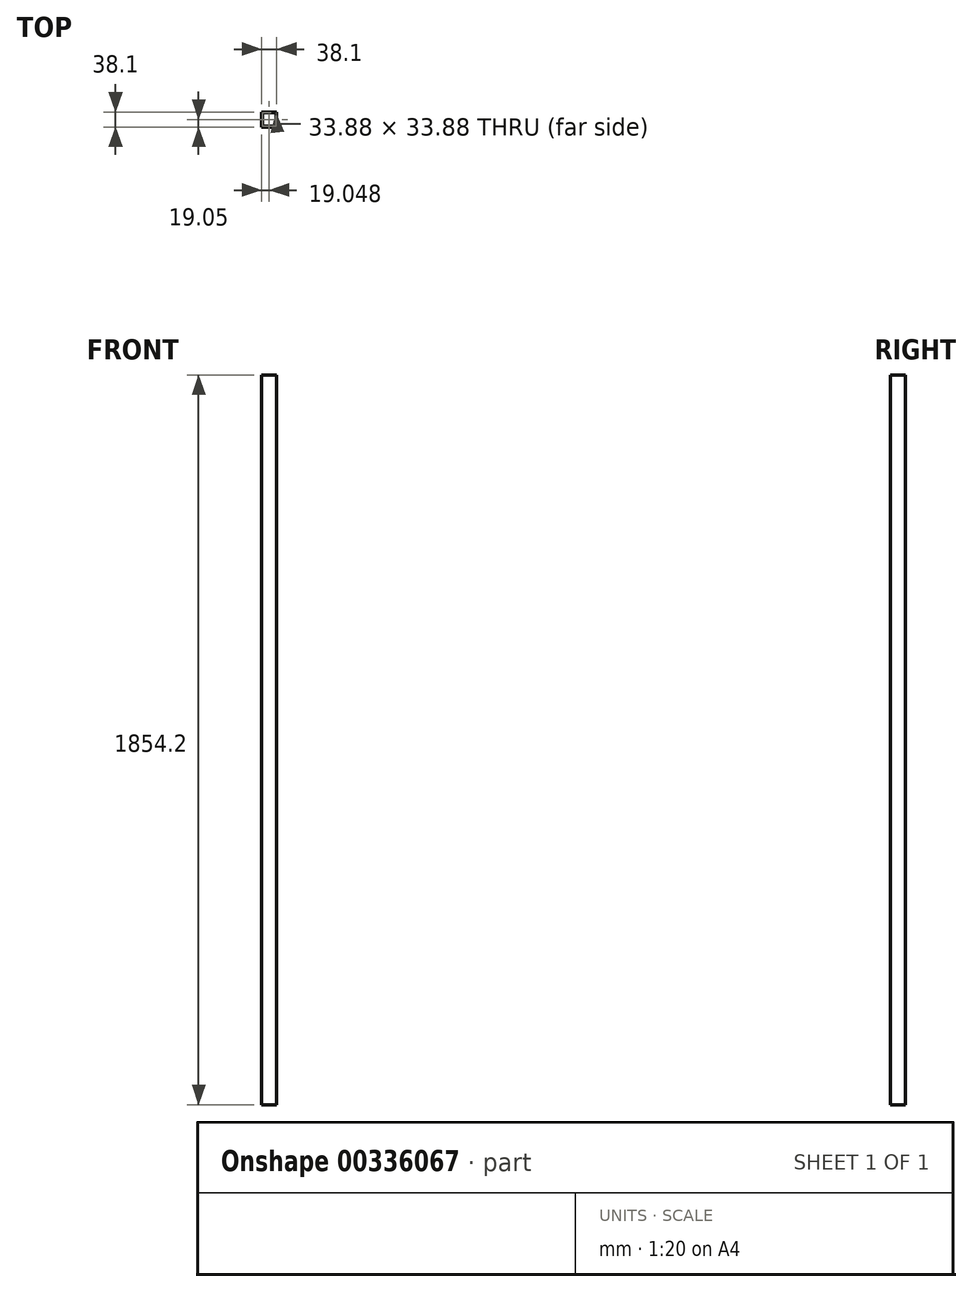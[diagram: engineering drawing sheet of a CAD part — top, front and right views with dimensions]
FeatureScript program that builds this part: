
annotation { "Feature Type Name" : "Feature", "Feature Type Description" : "" }
export const myFeature = defineFeature(function(context is Context, id is Id, definition is map)
    precondition{}
    {
        {
            var Q0;
            Q0=qCreatedBy(makeId("Front.planeOp"),FACE);
            var sketch = newSketch(context, id + "F0", { "sketchPlane" : qUnion([Q0])});
            skLineSegment(sketch, "E0.bottom", {"start": v(-146.7, 887.15) * mm, "end": v(-108.6, 887.15) * mm});
            skLineSegment(sketch, "E0.top", {"start": v(-146.7, -967.05) * mm, "end": v(-108.6, -967.05) * mm});
            skLineSegment(sketch, "E0.left", {"start": v(-146.7, 887.15) * mm, "end": v(-146.7, -967.05) * mm});
            skLineSegment(sketch, "E0.right", {"start": v(-108.6, 887.15) * mm, "end": v(-108.6, -967.05) * mm});
            skSolve(sketch);
        }
        {
            var Q0;
            Q0 = qSketchRegion(id + "F0", true);
            extrude(context, id + "F1", {"entities" : qUnion([Q0]), "depth" : 38.1 * mm});
        }
        {
            var Q0;
            Q0=makeQuery(id+"F1.opExtrude","SWEPT_FACE",FACE,{"disambiguationData":[OSD([sQuery(id+"F0.wireOp",EDGE,"E0.bottom")])]});
            var sketch = newSketch(context, id + "F2", { "sketchPlane" : qUnion([Q0])});
            skLineSegment(sketch, "E1.0", {"start": v(-144.6, -2.1) * mm, "end": v(-110.71, -2.1) * mm});
            skLineSegment(sketch, "E1.1", {"start": v(-144.6, -36) * mm, "end": v(-144.6, -2.1) * mm});
            skLineSegment(sketch, "E1.2", {"start": v(-144.6, -36) * mm, "end": v(-110.71, -36) * mm});
            skLineSegment(sketch, "E1.3", {"start": v(-110.71, -36) * mm, "end": v(-110.71, -2.1) * mm});
            skSolve(sketch);
        }
        {
            var Q0;
            Q0 = qSketchRegion(id + "F2", true);
            extrude(context, id + "F3", {"entities" : qUnion([Q0]), "operationType" : NewBodyOperationType.REMOVE, "oppositeDirection" : true, "depth" : 2032 * mm});
        }
    });
